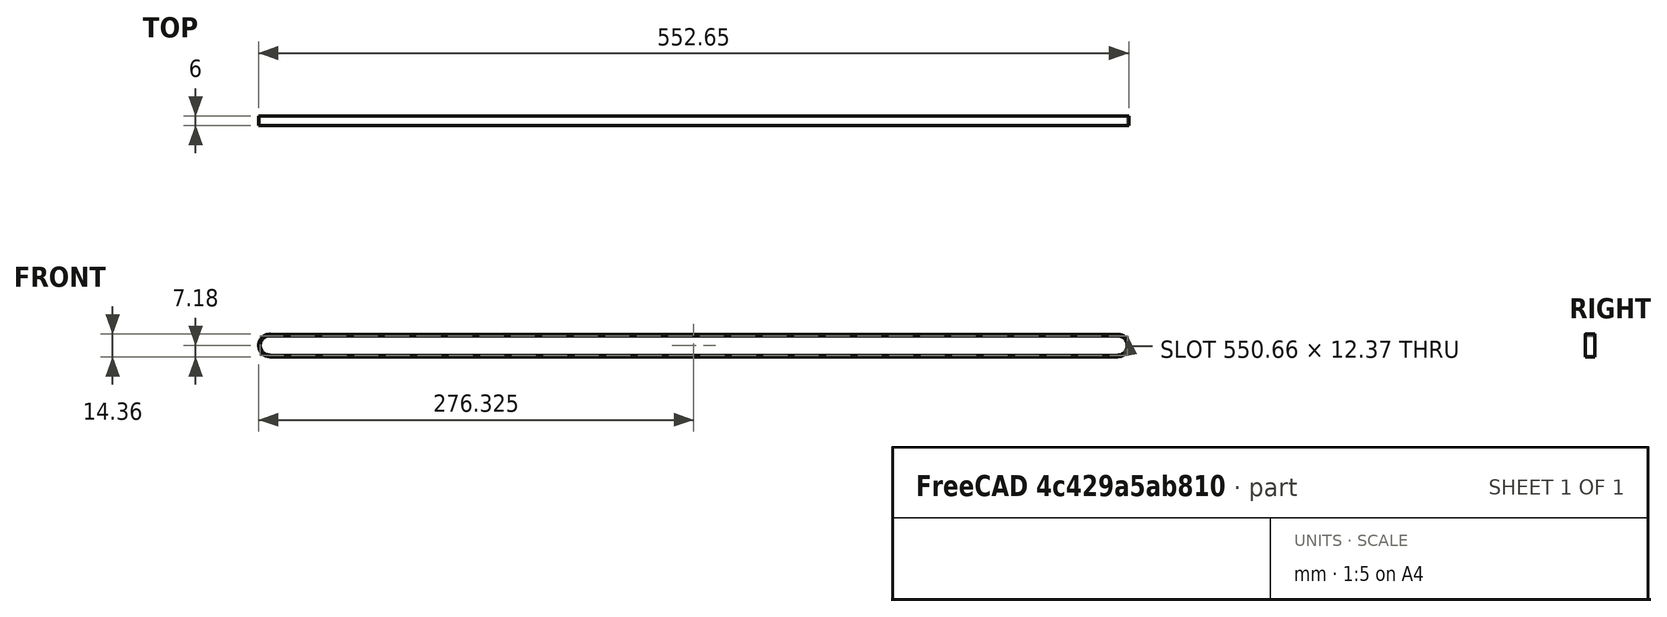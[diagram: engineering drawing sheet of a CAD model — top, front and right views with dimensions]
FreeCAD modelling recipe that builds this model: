
FCSTD DOCUMENT  (FreeCAD 0.19R21858 (Git))
Label: y_axis_2gt_belt
License: All rights reserved
LicenseURL: http://en.wikipedia.org/wiki/All_rights_reserved
objects: Sketcher::SketchObject×1, PartDesign::Pad×1, PartDesign::Body×1, App::Part×1
note: 4 computed .brp shape members not serialized (recipe doc carries the construction recipe); baked Part::Feature solids carry a one-line shape summary decoded from their .brp

FEATURE [Sketcher::SketchObject] Sketch022
  MapMode = 5
  Placement = pos=(0,0,0) rot=(1,0,0;1.5708rad)
  Support = -> [XZ_Plane028]
  sketch-geometry (8):
    g0: ArcOfCircle CenterX=0 CenterY=0 CenterZ=0 NormalX=0 NormalY=0 NormalZ=1 AngleXU=0 Radius=6.163 StartAngle=1.57072 EndAngle=4.71231
    g1: ArcOfCircle CenterX=538.33 CenterY=-0.04 CenterZ=0 NormalX=0 NormalY=0 NormalZ=1 AngleXU=0 Radius=6.163 StartAngle=4.71231 EndAngle=7.85391
    g2: LineSegment StartX=-0.000457935 StartY=-6.163 StartZ=0 EndX=538.33 EndY=-6.203 EndZ=0
    g3: LineSegment StartX=0.000457935 StartY=6.163 StartZ=0 EndX=538.33 EndY=6.123 EndZ=0
    g4: ArcOfCircle CenterX=0 CenterY=0 CenterZ=0 NormalX=0 NormalY=0 NormalZ=1 AngleXU=0 Radius=7.163 StartAngle=1.57072 EndAngle=4.71231
    g5: ArcOfCircle CenterX=538.33 CenterY=-0.04 CenterZ=0 NormalX=0 NormalY=0 NormalZ=1 AngleXU=0 Radius=7.163 StartAngle=4.71231 EndAngle=7.85391
    g6: LineSegment StartX=-0.000532239 StartY=-7.163 StartZ=0 EndX=538.329 EndY=-7.203 EndZ=0
    g7: LineSegment StartX=0.000532239 StartY=7.163 StartZ=0 EndX=538.331 EndY=7.123 EndZ=0
  constraints (17):
    c: Tangent(g0,g3) = 1.5708
    c: Tangent(g0,g2) = -1.5708
    c: Tangent(g2,g1) = -1.5708
    c: Tangent(g3,g1) = 1.5708
    c: Equal(g0,g1)
    c: Tangent(g4,g7) = 1.5708
    c: Tangent(g4,g6) = -1.5708
    c: Tangent(g6,g5) = -1.5708
    c: Tangent(g7,g5) = 1.5708
    c: Equal(g4,g5)
    c: Coincident(g4,g0)
    c: Coincident(g5,g1)
    c: Distance(g5,g1) = 1
    c: Radius(g4) = 7.163
    c: DistanceX(g0,g1) = 538.33
    c: DistanceY(g1,g0) = 0.04
    c: Coincident(g0,g-1)
FEATURE [PartDesign::Pad] Pad010
  AllowMultiFace = false
  Length = 6
  Length2 = 100
  Midplane = true
  Placement = pos=(0,0,0) rot=(1,0,0;1.5708rad)
  Profile = -> Sketch022
  Type = 0
FEATURE [PartDesign::Body] Body009  label="Body"
  Group = -> [Sketch022,Pad010]
  Origin = -> Origin028
  Tip = -> Pad010
FEATURE [App::Part] Part  label="y_axis_2gt_belt"
  Group = -> [Body009]
  Origin = -> Origin
